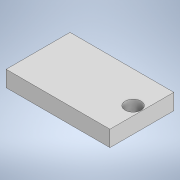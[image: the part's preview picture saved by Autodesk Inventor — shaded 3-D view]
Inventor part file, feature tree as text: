
AUTODESK INVENTOR PART (.ipt)
format: ipt  version: 2021 (Build 250183000, 183)  size: 104,448 bytes
history: native  units: mm
features: other x1, extrude x1, sketch x1
ambient origin geometry x8: Origin, YZ Plane, XZ Plane, XY Plane, X Axis, Y Axis, Z Axis, Center Point
bodies: Body1 (feature_tree)
feature tree (3):
  other  "Sólido1"
  extrude  "Extrusión1"  Depth=8.0mm
  sketch  "Boceto1"  dims[d0=13.0mm d1=8.0mm d2=2.0mm d3=1.1mm d4=4.0mm d5=4.0mm d6=2.0mm d7=0.0mm]
